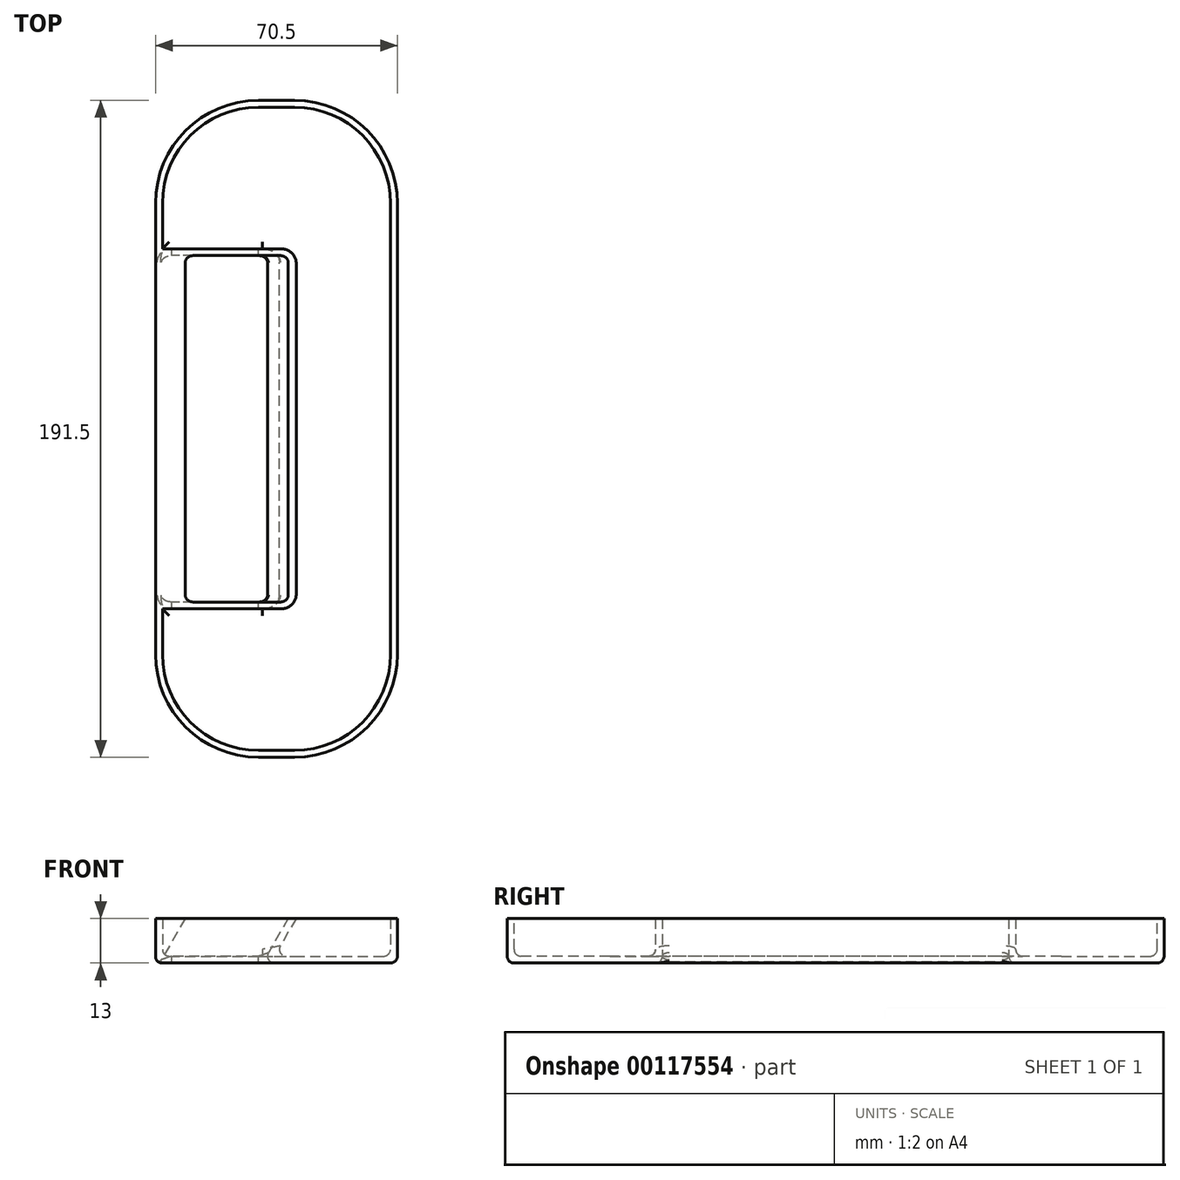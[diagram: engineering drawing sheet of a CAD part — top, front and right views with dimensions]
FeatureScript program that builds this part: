
annotation { "Feature Type Name" : "Feature", "Feature Type Description" : "" }
export const myFeature = defineFeature(function(context is Context, id is Id, definition is map)
    precondition{}
    {
        {
            var Q0;
            Q0=qCreatedBy(makeId("Top.planeOp"),FACE);
            var sketch = newSketch(context, id + "F0", { "sketchPlane" : qUnion([Q0])});
            skLineSegment(sketch, "E0.bottom", {"start": v(-5.25, 95.75) * mm, "end": v(5.25, 95.75) * mm});
            skLineSegment(sketch, "E0.top", {"start": v(-5.25, -95.75) * mm, "end": v(5.25, -95.75) * mm});
            skLineSegment(sketch, "E0.left", {"start": v(-35.25, 65.75) * mm, "end": v(-35.25, -65.75) * mm});
            skLineSegment(sketch, "E0.right", {"start": v(35.25, 65.75) * mm, "end": v(35.25, -65.75) * mm});
            skLineSegment(sketch, "E1", {"start": v(-35.25, 0) * mm, "end": v(35.25, 0) * mm, "construction": true});
            skPoint(sketch, "E2.visualSharp", {"position": v(-35.25, 95.75) * mm});
            skArc(sketch, "E2.filletArc", {"start": v(-5.25, 95.75) * mm, "mid": v(-26.46, 86.96) * mm, "end": v(-35.25, 65.75) * mm});
            skPoint(sketch, "E3.visualSharp", {"position": v(-35.25, -95.75) * mm});
            skArc(sketch, "E3.filletArc", {"start": v(-35.25, -65.75) * mm, "mid": v(-26.46, -86.96) * mm, "end": v(-5.25, -95.75) * mm});
            skPoint(sketch, "E4.visualSharp", {"position": v(35.25, -95.75) * mm});
            skArc(sketch, "E4.filletArc", {"start": v(5.25, -95.75) * mm, "mid": v(26.46, -86.96) * mm, "end": v(35.25, -65.75) * mm});
            skPoint(sketch, "E5.visualSharp", {"position": v(35.25, 95.75) * mm});
            skArc(sketch, "E5.filletArc", {"start": v(35.25, 65.75) * mm, "mid": v(26.46, 86.96) * mm, "end": v(5.25, 95.75) * mm});
            skLineSegment(sketch, "E6", {"start": v(0, -95.75) * mm, "end": v(0, 95.75) * mm, "construction": true});
            skSolve(sketch);
        }
        {
            var Q0;
            Q0=qSketchRegion(id+"F0",true);
            extrude(context, id + "F1", {"entities" : qUnion([Q0]), "depth" : 13 * mm});
        }
        {
            var Q0;
            Q0=sQuery(id+"F0.wireOp",EDGE,"E6");
            cPlane(context, id + "F2", {"entities" : qUnion([Q0]), "cplaneType" : CPlaneType.LINE_ANGLE, "offset" : 150 * mm, "angle" : 30 * degree, "width" : 150 * mm, "height" : 150 * mm});
        }
        {
            var Q0;
            Q0=qCreatedBy(id+"F2.planeOp",FACE);
            var sketch = newSketch(context, id + "F3", { "sketchPlane" : qUnion([Q0])});
            skLineSegment(sketch, "E7.bottom", {"start": v(-29.53, 50.5) * mm, "end": v(-3.53, 50.5) * mm});
            skLineSegment(sketch, "E7.top", {"start": v(-29.53, -50.5) * mm, "end": v(-3.53, -50.5) * mm});
            skLineSegment(sketch, "E7.left", {"start": v(-29.53, 50.5) * mm, "end": v(-29.53, -50.5) * mm});
            skLineSegment(sketch, "E7.right", {"start": v(-3.53, 50.5) * mm, "end": v(-3.53, -50.5) * mm});
            skLineSegment(sketch, "E8", {"start": v(0, 0) * mm, "end": v(-3.53, 0) * mm, "construction": true});
            skSolve(sketch);
        }
        {
            var Q0;
            Q0=qSketchRegion(id+"F3",true);
            extrude(context, id + "F4", {"entities" : qUnion([Q0]), "operationType" : NewBodyOperationType.REMOVE, "endBound" : BoundingType.THROUGH_ALL, "depth" : 25 * mm, "hasSecondDirection" : true, "secondDirectionBound" : BoundingType.THROUGH_ALL, "secondDirectionOppositeDirection" : true, "secondDirectionDepth" : 25 * mm});
        }
        {
            var Q0;
            Q0=makeQuery(id+"F4.boolean.opBoolean","COPY",EDGE,{"derivedFrom":makeQuery(id+"F4.opExtrude","SWEPT_EDGE",EDGE,{"disambiguationData":[OSD([sQuery(id+"F3.wireOp",EDGE,"E7.top"),sQuery(id+"F3.wireOp",EDGE,"E7.left")])]})});
            var Q1;
            Q1=makeQuery(id+"F4.boolean.opBoolean","COPY",EDGE,{"derivedFrom":makeQuery(id+"F4.opExtrude","SWEPT_EDGE",EDGE,{"disambiguationData":[OSD([sQuery(id+"F3.wireOp",EDGE,"E7.bottom"),sQuery(id+"F3.wireOp",EDGE,"E7.left")])]})});
            var Q2;
            Q2=makeQuery(id+"F4.boolean.opBoolean","COPY",EDGE,{"derivedFrom":makeQuery(id+"F4.opExtrude","SWEPT_EDGE",EDGE,{"disambiguationData":[OSD([sQuery(id+"F3.wireOp",EDGE,"E7.bottom"),sQuery(id+"F3.wireOp",EDGE,"E7.right")])]})});
            var Q3;
            Q3=makeQuery(id+"F4.boolean.opBoolean","COPY",EDGE,{"derivedFrom":makeQuery(id+"F4.opExtrude","SWEPT_EDGE",EDGE,{"disambiguationData":[OSD([sQuery(id+"F3.wireOp",EDGE,"E7.top"),sQuery(id+"F3.wireOp",EDGE,"E7.right")])]})});
            var Q4;
            Q4=makeQuery(id+"F1.opExtrude","CAP_FACE",FACE,{"disambiguationData":[OSD([sQuery(id+"F0.wireOp",EDGE,"E0.bottom"),sQuery(id+"F0.wireOp",EDGE,"E0.top"),sQuery(id+"F0.wireOp",EDGE,"E0.left"),sQuery(id+"F0.wireOp",EDGE,"E0.right"),sQuery(id+"F0.wireOp",EDGE,"E2.filletArc"),sQuery(id+"F0.wireOp",EDGE,"E3.filletArc"),sQuery(id+"F0.wireOp",EDGE,"E4.filletArc"),sQuery(id+"F0.wireOp",EDGE,"E5.filletArc")])],"isStart":true});
            fillet(context, id + "F5", {"entities" : qUnion([Q0, Q1, Q2, Q3, Q4]), "radius" : 2 * mm, "tangentPropagation" : true, "allowEdgeOverflow" : false});
        }
        {
            var Q0;
            {var subQ0=sQuery(id+"F0.wireOp",EDGE,"E0.left");Q0=makeQuery(id+"F5.opFillet","BLEND_EDGE",EDGE,{"blendedFrom":[makeQuery(id+"F1.opExtrude","CAP_EDGE",EDGE,{"disambiguationData":[OSD([subQ0])],"isStart":true}),makeQuery(id+"F4.boolean.opBoolean","INTERSECT",EDGE,{"derivedFrom":[makeQuery(id+"F1.opExtrude","CAP_FACE",FACE,{"disambiguationData":[OSD([sQuery(id+"F0.wireOp",EDGE,"E0.bottom"),sQuery(id+"F0.wireOp",EDGE,"E0.top"),subQ0,sQuery(id+"F0.wireOp",EDGE,"E0.right"),sQuery(id+"F0.wireOp",EDGE,"E2.filletArc"),sQuery(id+"F0.wireOp",EDGE,"E3.filletArc"),sQuery(id+"F0.wireOp",EDGE,"E4.filletArc"),sQuery(id+"F0.wireOp",EDGE,"E5.filletArc")])],"isStart":true}),makeQuery(id+"F4.opExtrude","SWEPT_FACE",FACE,{"disambiguationData":[OSD([sQuery(id+"F3.wireOp",EDGE,"E7.bottom")])]})]})],"blendedInto":[]});}
            var Q1;
            {var subQ0=sQuery(id+"F0.wireOp",EDGE,"E0.left");Q1=makeQuery(id+"F5.opFillet","BLEND_EDGE",EDGE,{"disambiguationData":[OD(0.0)],"blendedFrom":[makeQuery(id+"F1.opExtrude","CAP_EDGE",EDGE,{"disambiguationData":[OSD([subQ0])],"isStart":true}),makeQuery(id+"F4.boolean.opBoolean","INTERSECT",EDGE,{"derivedFrom":[makeQuery(id+"F1.opExtrude","CAP_FACE",FACE,{"disambiguationData":[OSD([sQuery(id+"F0.wireOp",EDGE,"E0.bottom"),sQuery(id+"F0.wireOp",EDGE,"E0.top"),subQ0,sQuery(id+"F0.wireOp",EDGE,"E0.right"),sQuery(id+"F0.wireOp",EDGE,"E2.filletArc"),sQuery(id+"F0.wireOp",EDGE,"E3.filletArc"),sQuery(id+"F0.wireOp",EDGE,"E4.filletArc"),sQuery(id+"F0.wireOp",EDGE,"E5.filletArc")])],"isStart":true}),makeQuery(id+"F4.opExtrude","SWEPT_FACE",FACE,{"disambiguationData":[OSD([sQuery(id+"F3.wireOp",EDGE,"E7.left")])]})]})],"blendedInto":[]});}
            var Q2;
            {var subQ0=sQuery(id+"F0.wireOp",EDGE,"E0.left");Q2=makeQuery(id+"F5.opFillet","BLEND_EDGE",EDGE,{"disambiguationData":[OD(1.0)],"blendedFrom":[makeQuery(id+"F1.opExtrude","CAP_EDGE",EDGE,{"disambiguationData":[OSD([subQ0])],"isStart":true}),makeQuery(id+"F4.boolean.opBoolean","INTERSECT",EDGE,{"derivedFrom":[makeQuery(id+"F1.opExtrude","CAP_FACE",FACE,{"disambiguationData":[OSD([sQuery(id+"F0.wireOp",EDGE,"E0.bottom"),sQuery(id+"F0.wireOp",EDGE,"E0.top"),subQ0,sQuery(id+"F0.wireOp",EDGE,"E0.right"),sQuery(id+"F0.wireOp",EDGE,"E2.filletArc"),sQuery(id+"F0.wireOp",EDGE,"E3.filletArc"),sQuery(id+"F0.wireOp",EDGE,"E4.filletArc"),sQuery(id+"F0.wireOp",EDGE,"E5.filletArc")])],"isStart":true}),makeQuery(id+"F4.opExtrude","SWEPT_FACE",FACE,{"disambiguationData":[OSD([sQuery(id+"F3.wireOp",EDGE,"E7.left")])]})]})],"blendedInto":[]});}
            fillet(context, id + "F6", {"entities" : qUnion([Q0, Q1, Q2]), "radius" : .7 * mm, "tangentPropagation" : true, "allowEdgeOverflow" : false});
        }
        {
            var Q0;
            Q0=makeQuery(id+"F1.opExtrude","CAP_FACE",FACE,{"disambiguationData":[OSD([sQuery(id+"F0.wireOp",EDGE,"E0.bottom"),sQuery(id+"F0.wireOp",EDGE,"E0.top"),sQuery(id+"F0.wireOp",EDGE,"E0.left"),sQuery(id+"F0.wireOp",EDGE,"E0.right"),sQuery(id+"F0.wireOp",EDGE,"E2.filletArc"),sQuery(id+"F0.wireOp",EDGE,"E3.filletArc"),sQuery(id+"F0.wireOp",EDGE,"E4.filletArc"),sQuery(id+"F0.wireOp",EDGE,"E5.filletArc")])],"isStart":false});
            shell(context, id + "F7", {"entities" : qUnion([Q0]), "thickness" : 2 * mm});
        }
        {
            var Q0;
            Q0=makeQuery(id+"F7.opShell","OFFSET_FACE",FACE,{"disambiguationData":[OSD([sQuery(id+"F3.wireOp",EDGE,"E7.bottom")])]});
            var sketch = newSketch(context, id + "F8", { "sketchPlane" : qUnion([Q0])});
            skLineSegment(sketch, "E9.0", {"start": v(24.28, 13) * mm, "end": v(30.63, 2) * mm});
            skLineSegment(sketch, "E10", {"start": v(24.28, 13) * mm, "end": v(33.25, 13) * mm});
            skLineSegment(sketch, "E11", {"start": v(33.25, 13) * mm, "end": v(33.25, 2) * mm});
            skLineSegment(sketch, "E12", {"start": v(33.25, 2) * mm, "end": v(30.63, 2) * mm});
            skSolve(sketch);
        }
        {
            var Q0;
            Q0=qSketchRegion(id+"F8",true);
            var Q1;
            Q1=makeQuery(id+"F4.boolean.opBoolean","COPY",FACE,{"derivedFrom":makeQuery(id+"F4.opExtrude","SWEPT_FACE",FACE,{"disambiguationData":[OSD([sQuery(id+"F3.wireOp",EDGE,"E7.bottom")])]})});
            extrude(context, id + "F9", {"entities" : qUnion([Q0]), "endBound" : BoundingType.UP_TO_SURFACE, "oppositeDirection" : true, "endBoundEntityFace" : qUnion([Q1]), "depth" : 25 * mm});
        }
        {
            var Q0;
            Q0=makeQuery(id+"F9.opExtrude","SWEPT_BODY",BODY,{"disambiguationData":[OSD([sQuery(id+"F8.wireOp",EDGE,"E9.0"),sQuery(id+"F8.wireOp",EDGE,"E10"),sQuery(id+"F8.wireOp",EDGE,"E11"),sQuery(id+"F8.wireOp",EDGE,"E12")])]});
            var Q1;
            Q1=qCreatedBy(makeId("Front.planeOp"),FACE);
            mirror(context, id + "F10", {"operationType" : NewBodyOperationType.ADD, "entities" : qUnion([Q0]), "mirrorPlane" : qUnion([Q1])});
        }
        {
            var Q0;
            Q0=makeQuery(id+"F7.opShell","OFFSET_FACE",FACE,{"disambiguationData":[OSD([sQuery(id+"F3.wireOp",EDGE,"E7.bottom")])]});
            var sketch = newSketch(context, id + "F11", { "sketchPlane" : qUnion([Q0])});
            skLineSegment(sketch, "E13.0", {"start": v(33.25, 1.46) * mm, "end": v(26.59, 13) * mm});
            skLineSegment(sketch, "E14", {"start": v(26.59, 13) * mm, "end": v(33.25, 13) * mm});
            skLineSegment(sketch, "E15", {"start": v(33.25, 13) * mm, "end": v(33.25, 1.46) * mm});
            skSolve(sketch);
        }
        {
            var Q0;
            Q0=qSketchRegion(id+"F11",true);
            var Q1;
            Q1=makeQuery(id+"F4.boolean.opBoolean","COPY",FACE,{"derivedFrom":makeQuery(id+"F4.opExtrude","SWEPT_FACE",FACE,{"disambiguationData":[OSD([sQuery(id+"F3.wireOp",EDGE,"E7.top")])]})});
            extrude(context, id + "F12", {"entities" : qUnion([Q0]), "operationType" : NewBodyOperationType.ADD, "endBound" : BoundingType.UP_TO_SURFACE, "oppositeDirection" : true, "endBoundEntityFace" : qUnion([Q1]), "depth" : 97.92 * mm});
        }
        {
            var Q0;
            {var subQ0=sQuery(id+"F0.wireOp",EDGE,"E5.filletArc");var subQ1=sQuery(id+"F0.wireOp",EDGE,"E4.filletArc");var subQ2=sQuery(id+"F0.wireOp",EDGE,"E3.filletArc");var subQ3=sQuery(id+"F0.wireOp",EDGE,"E2.filletArc");var subQ4=sQuery(id+"F0.wireOp",EDGE,"E0.right");var subQ5=sQuery(id+"F0.wireOp",EDGE,"E0.left");var subQ6=sQuery(id+"F0.wireOp",EDGE,"E0.top");var subQ7=sQuery(id+"F0.wireOp",EDGE,"E0.bottom");Q0=makeQuery(id+"F7.opShell","OFFSET_FACE",FACE,{"disambiguationData":[OSD([subQ7,subQ6,subQ5,subQ4,subQ3,subQ2,subQ1,subQ0]),TDD([makeQuery(id+"F1.opExtrude","CAP_FACE",FACE,{"disambiguationData":[OSD([subQ7,subQ6,subQ5,subQ4,subQ3,subQ2,subQ1,subQ0])],"isStart":true})])]});}
            var Q1;
            Q1=makeQuery(id+"F9.opExtrude","CAP_EDGE",EDGE,{"disambiguationData":[OSD([sQuery(id+"F8.wireOp",EDGE,"E11")])],"isStart":true});
            var Q2;
            Q2=makeQuery(id+"F10.opPattern","COPY",EDGE,{"derivedFrom":makeQuery(id+"F9.opExtrude","CAP_EDGE",EDGE,{"disambiguationData":[OSD([sQuery(id+"F8.wireOp",EDGE,"E11")])],"isStart":true}),"instanceName":"1"});
            fillet(context, id + "F13", {"entities" : qUnion([Q0, Q1, Q2]), "radius" : 2 * mm, "tangentPropagation" : true, "allowEdgeOverflow" : false});
        }
    });
